# Revit family: EDE-GRF-DCH-Shelby Llave Pared Pico Alt Cocina Cromo
name_source: partatom
category: Aparatos sanitarios
units: mm (PartAtom-declared; Revit-internal decimal feet)

## family parameters
Anfitrión = Muro
Compartido = No
Corte con vacíos al cargar = No
Cota de conector redondo = Diámetro de uso
Número OmniClass = 23.45.00.00
Punto de cálculo de habitación = No
Siempre vertical = Sí
Tipo de pieza = Normal
Título OmniClass = Sanitary, Laundry, and Cleaning Equipment

## types (1)
- SHELBY LLAVE DE PARED PICO ALTO PARA COCINA
    Fabricante = EDESA-PREMIUM
    Modelo = SHELBY LLAVE DE PARED PICO ALTO PARA COCINA
    URL = https://www.edesa.com.ec
    _ALT_ Conexión = 1 m
    _EDESA_ Alto en cm = 16
    _EDESA_ Ancho en cm = 8
    _EDESA_ Categoría = Productos > Grifería > Cocina
    _EDESA_ Certificación = Cumple con norma NTE - INEN 3123 basada en la norma ASME 112.18.1 - 2012.
    _EDESA_ Color = cromo
    _EDESA_ Conexión Hidráulica = Entrada de agua: tubería ø 1/2"
    _EDESA_ Consumo/capacidad de agua en L = 8.3 litros por minuto / 2.2 gpm a 60 psi
    _EDESA_ Descripción = Llave de cocina para agua fría. Instalación a la pared. Incluye desagüe y sifón.
    _EDESA_ Garantía = De por vida para el cuerpo principal y acabado en cromo (306)
    _EDESA_ Manual de instalación = https://www.edesa.com.ec
    _EDESA_ Marca = EDESA
    _EDESA_ Materiales = Latón
    _EDESA_ Nombre = SHELBY LLAVE DE PARED PICO ALTO PARA COCINA
    _EDESA_ Productos incluídos = Desagüe 1 1/2” PP con rejilla, Sifón 1 1/2” de Plástico con Acople
    _EDESA_ Profundidad en cm = 24
    _EDESA_ Sku/código = SG0074303061CE
    _EDESA_ Tipo de instalación = A la pared
